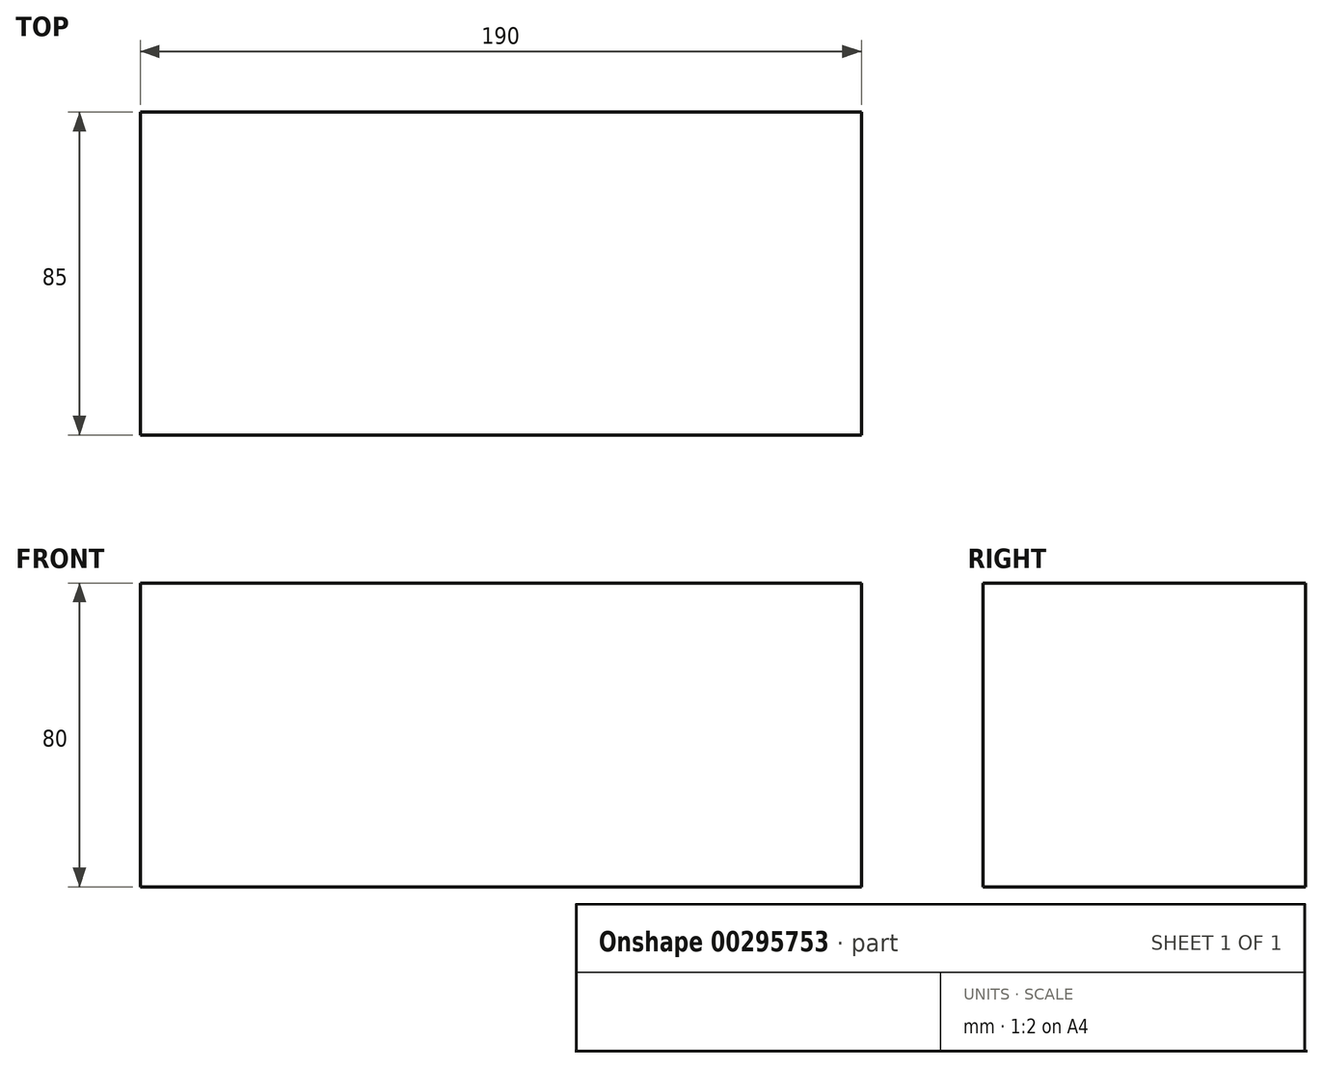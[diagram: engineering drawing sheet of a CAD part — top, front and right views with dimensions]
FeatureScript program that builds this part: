
annotation { "Feature Type Name" : "Feature", "Feature Type Description" : "" }
export const myFeature = defineFeature(function(context is Context, id is Id, definition is map)
    precondition{}
    {
        {
            var Q0;
            Q0=qCreatedBy(makeId("Top.planeOp"),FACE);
            var sketch = newSketch(context, id + "F0", { "sketchPlane" : qUnion([Q0])});
            skLineSegment(sketch, "E0.bottom", {"start": v(-114.05, 32.77) * mm, "end": v(75.95, 32.77) * mm});
            skLineSegment(sketch, "E0.top", {"start": v(-114.05, -52.23) * mm, "end": v(75.95, -52.23) * mm});
            skLineSegment(sketch, "E0.left", {"start": v(-114.05, 32.77) * mm, "end": v(-114.05, -52.23) * mm});
            skLineSegment(sketch, "E0.right", {"start": v(75.95, 32.77) * mm, "end": v(75.95, -52.23) * mm});
            skSolve(sketch);
        }
        {
            var Q0;
            Q0 = qSketchRegion(id + "F0", true);
            extrude(context, id + "F1", {"entities" : qUnion([Q0]), "depth" : 80 * mm});
        }
    });
